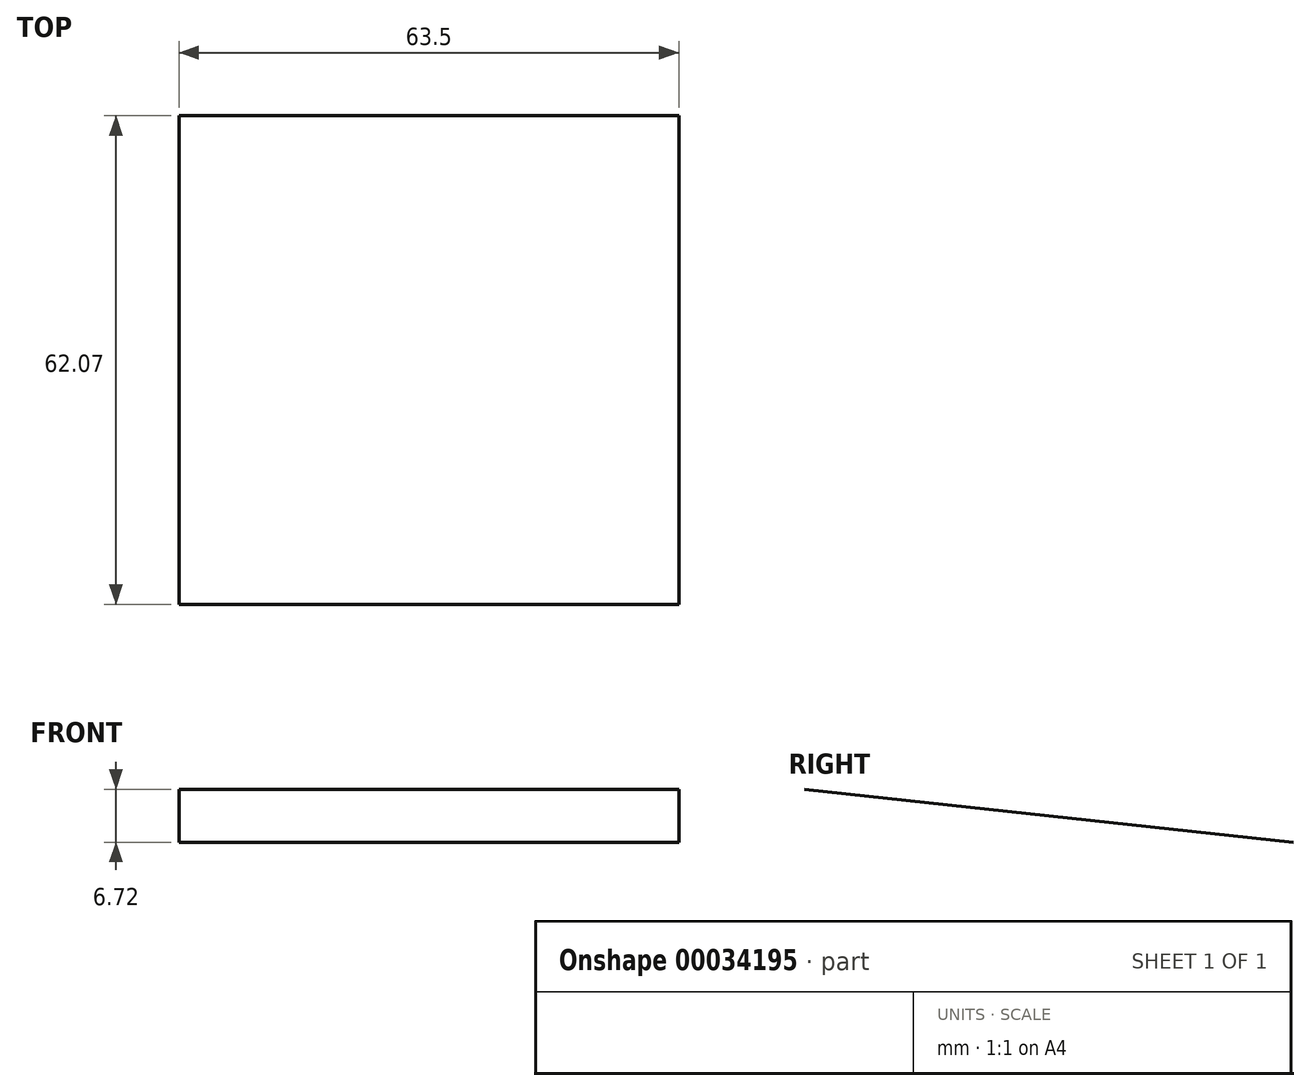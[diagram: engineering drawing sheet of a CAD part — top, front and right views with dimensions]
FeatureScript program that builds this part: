
annotation { "Feature Type Name" : "Feature", "Feature Type Description" : "" }
export const myFeature = defineFeature(function(context is Context, id is Id, definition is map)
    precondition{}
    {
        {
            var Q0;
            Q0=qCreatedBy(makeId("Right.planeOp"),FACE);
            var sketch = newSketch(context, id + "F0", { "sketchPlane" : qUnion([Q0])});
            skLineSegment(sketch, "E0", {"start": v(-27.27, 21.7) * mm, "end": v(-23.5, 17.93) * mm});
            skLineSegment(sketch, "E1", {"start": v(-10.5, 0) * mm, "end": v(34.8, 14.97) * mm});
            skLineSegment(sketch, "E2", {"start": v(34.8, 14.97) * mm, "end": v(-27.27, 21.7) * mm});
            skSolve(sketch);
        }
        {
            var Q0;
            Q0=sQuery(id+"F0.wireOp",EDGE,"E2");
            extrude(context, id + "F1", {"bodyType" : ToolBodyType.SURFACE, "surfaceEntities" : qUnion([Q0]), "depth" : 63.5 * mm, "offsetDistance" : 25.4 * mm});
        }
    });
